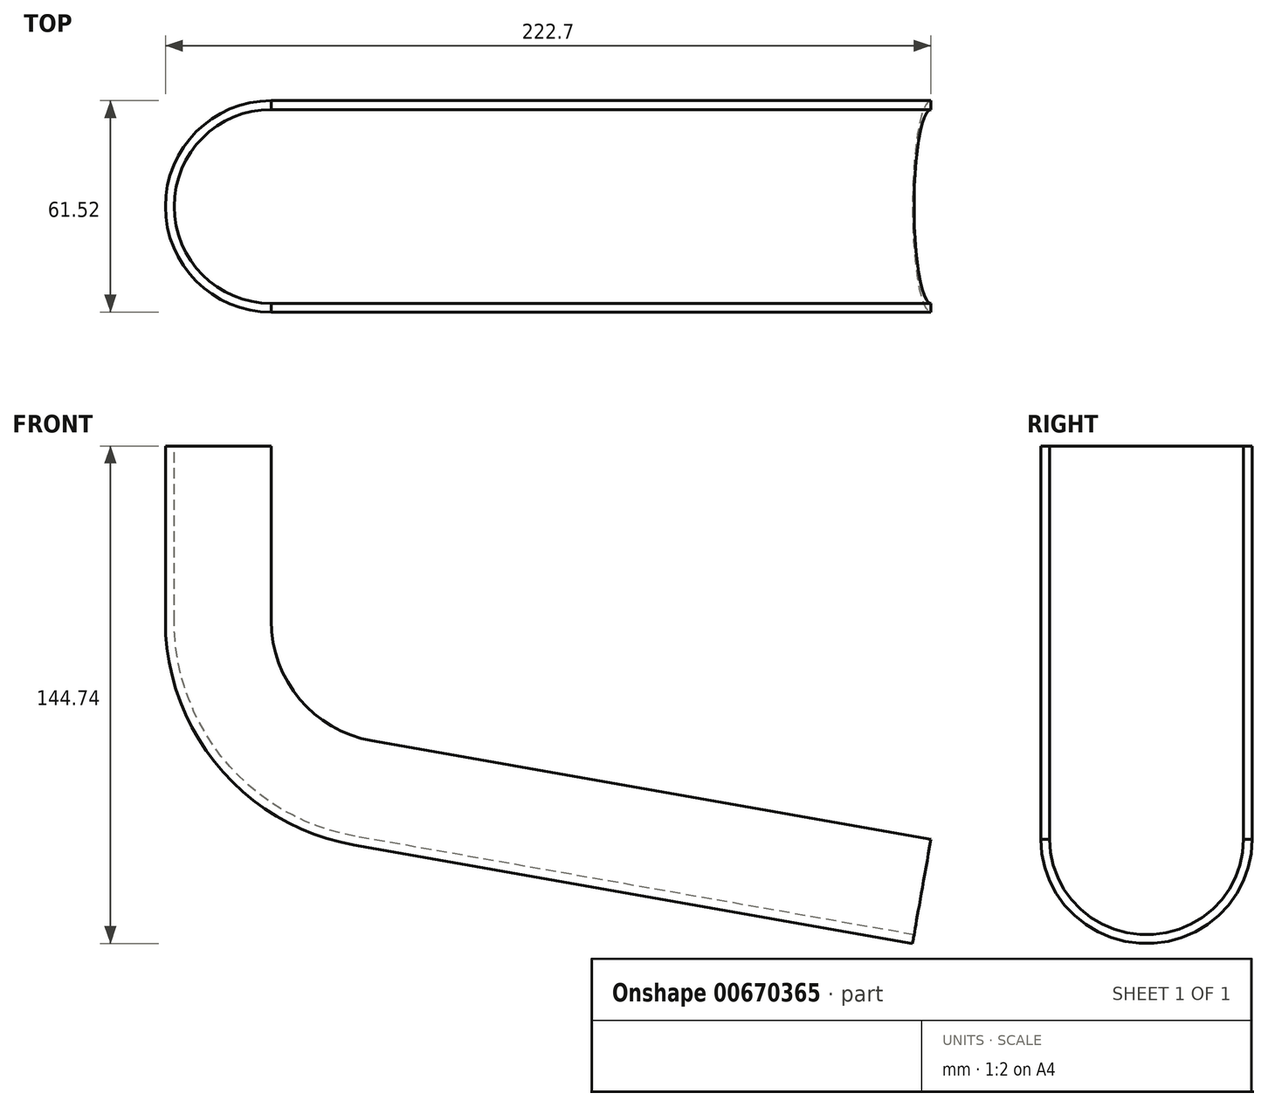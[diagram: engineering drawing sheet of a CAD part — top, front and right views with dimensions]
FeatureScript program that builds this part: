
annotation { "Feature Type Name" : "Feature", "Feature Type Description" : "" }
export const myFeature = defineFeature(function(context is Context, id is Id, definition is map)
    precondition{}
    {
        {
            var Q0;
            Q0=qCreatedBy(makeId("Front.planeOp"),FACE);
            var sketch = newSketch(context, id + "F0", { "sketchPlane" : qUnion([Q0])});
            skLineSegment(sketch, "E0", {"start": v(0, 0) * mm, "end": v(-35.56, 0) * mm, "construction": true});
            skLineSegment(sketch, "E1", {"start": v(0, 0) * mm, "end": v(-6.17, -35.02) * mm, "construction": true});
            skArc(sketch, "E2", {"start": v(-35.56, 0) * mm, "mid": v(-27.24, -22.86) * mm, "end": v(-6.17, -35.02) * mm});
            skLineSegment(sketch, "E3", {"start": v(-35.56, 0) * mm, "end": v(-35.56, 50.8) * mm});
            skLineSegment(sketch, "E4", {"start": v(-6.17, -35.02) * mm, "end": v(156.42, -63.69) * mm});
            skSolve(sketch);
        }
        {
            var Q0;
            Q0=qCreatedBy(makeId("Top.planeOp"),FACE);
            var sketch = newSketch(context, id + "F1", { "sketchPlane" : qUnion([Q0])});
            skArc(sketch, "E5", {"start": v(-35.51, 30.76) * mm, "mid": v(-66.28, 0) * mm, "end": v(-35.51, -30.76) * mm});
            skArc(sketch, "E6", {"start": v(-35.51, 28.2) * mm, "mid": v(-63.72, 0) * mm, "end": v(-35.51, -28.2) * mm});
            skLineSegment(sketch, "E7", {"start": v(-35.51, -30.76) * mm, "end": v(-35.51, -28.2) * mm});
            skLineSegment(sketch, "E8", {"start": v(-35.51, 30.76) * mm, "end": v(-35.51, 28.2) * mm});
            skSolve(sketch);
        }
        {
            var Q0;
            Q0 = qSketchRegion(id + "F1", true);
            var Q1;
            Q1 = qConstructionFilter(qBodyType(qCreatedBy(id + "F0" ,EDGE), BodyType.WIRE), ConstructionObject.NO);
            sweep(context, id + "F2", {"profiles" : qUnion([Q0]), "path" : qUnion([Q1])});
        }
    });
